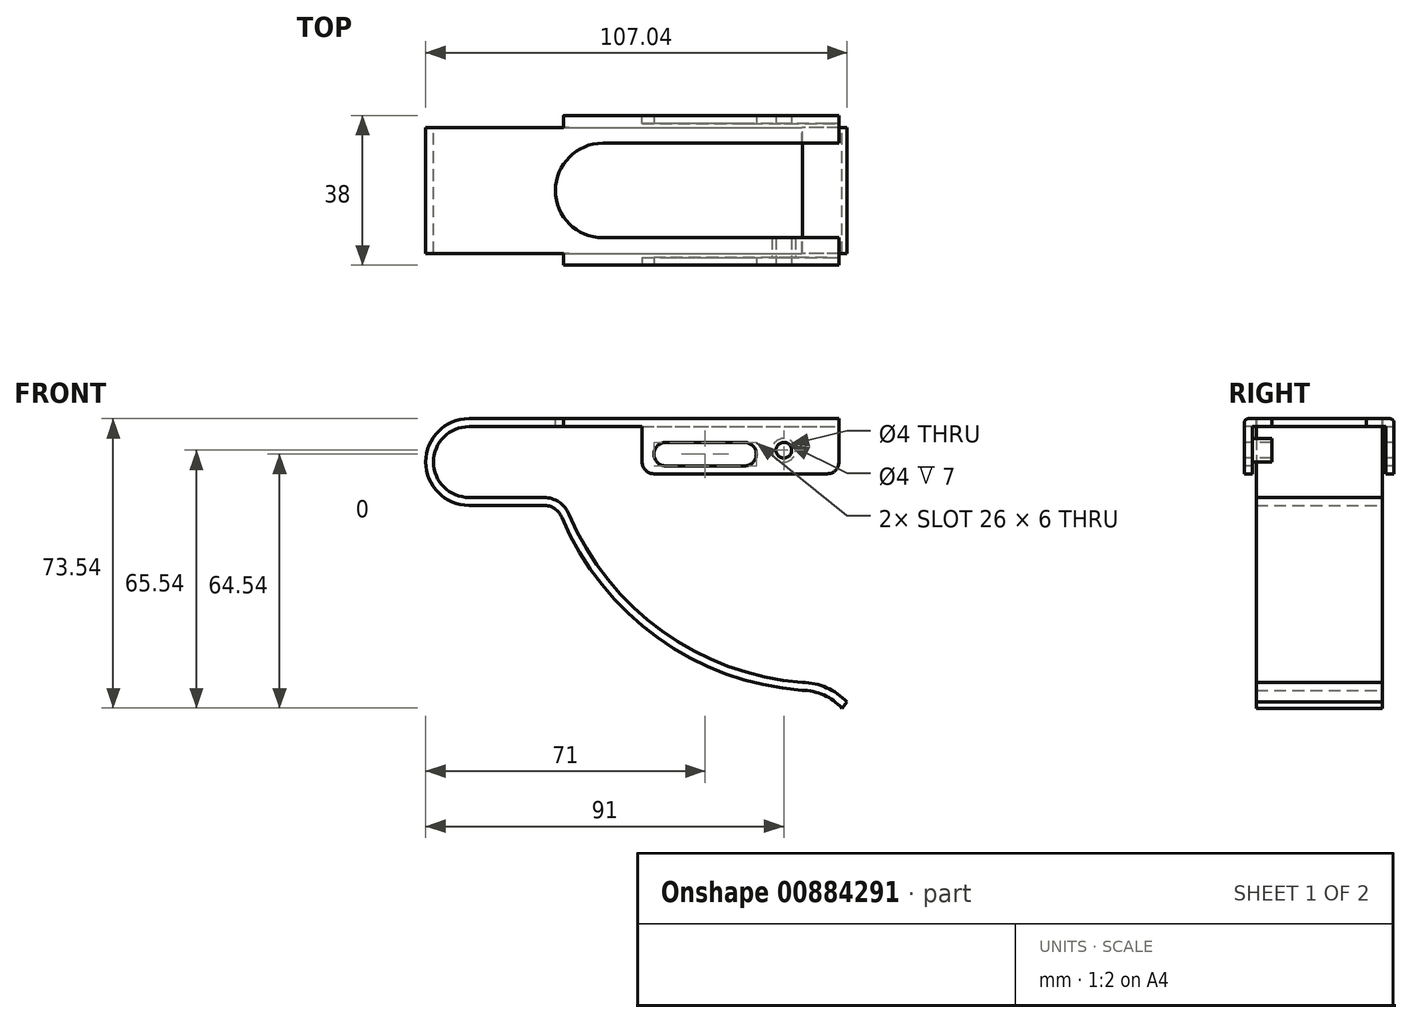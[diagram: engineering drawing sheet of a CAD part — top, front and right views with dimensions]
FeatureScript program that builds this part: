
annotation { "Feature Type Name" : "Feature", "Feature Type Description" : "" }
export const myFeature = defineFeature(function(context is Context, id is Id, definition is map)
    precondition{}
    {
        {
            var Q0;
            Q0=qCreatedBy(makeId("Front.planeOp"),FACE);
            var sketch = newSketch(context, id + "F0", { "sketchPlane" : qUnion([Q0])});
            skArc(sketch, "E0", {"start": v(0, 11) * mm, "mid": v(-11, 0) * mm, "end": v(0, -11) * mm});
            skLineSegment(sketch, "E1", {"start": v(0, 11) * mm, "end": v(94, 11) * mm});
            skLineSegment(sketch, "E2", {"start": v(0, -11) * mm, "end": v(19, -11) * mm});
            skArc(sketch, "E3", {"start": v(23.61, -14.06) * mm, "mid": v(47.92, -44.63) * mm, "end": v(84.61, -58) * mm});
            skPoint(sketch, "E4.visualSharp", {"position": v(22.4, -11) * mm});
            skArc(sketch, "E4.filletArc", {"start": v(23.61, -14.06) * mm, "mid": v(21.77, -11.84) * mm, "end": v(19, -11) * mm});
            skArc(sketch, "E5", {"start": v(94.75, -62.54) * mm, "mid": v(90.15, -59.22) * mm, "end": v(84.61, -58) * mm});
            skLineSegment(sketch, "E6.0", {"start": v(0, 9) * mm, "end": v(94, 9) * mm});
            skArc(sketch, "E6.1", {"start": v(0, 9) * mm, "mid": v(-9, 0) * mm, "end": v(0, -9) * mm});
            skArc(sketch, "E6.2", {"start": v(96.04, -61) * mm, "mid": v(90.88, -57.36) * mm, "end": v(84.7, -56) * mm});
            skArc(sketch, "E6.3", {"start": v(25.45, -13.3) * mm, "mid": v(49.07, -42.99) * mm, "end": v(84.7, -56) * mm});
            skArc(sketch, "E6.4", {"start": v(25.45, -13.3) * mm, "mid": v(22.88, -10.17) * mm, "end": v(19, -9) * mm});
            skLineSegment(sketch, "E6.5", {"start": v(0, -9) * mm, "end": v(19, -9) * mm});
            skLineSegment(sketch, "E7", {"start": v(94, 11) * mm, "end": v(94, 9) * mm});
            skLineSegment(sketch, "E8", {"start": v(96.04, -61) * mm, "end": v(94.75, -62.54) * mm});
            skLineSegment(sketch, "E9", {"start": v(96.04, -61) * mm, "end": v(104.04, -61) * mm, "construction": true});
            skSolve(sketch);
        }
        {
            var Q0;
            Q0=qSketchRegion(id+"F0",true);
            extrude(context, id + "F1", {"entities" : qUnion([Q0]), "depth" : 16 * mm, "offsetDistance" : 25 * mm});
        }
        {
            var Q0;
            Q0=makeQuery(id+"F1.opExtrude","SWEPT_FACE",FACE,{"disambiguationData":[OSD([sQuery(id+"F0.wireOp",EDGE,"E1")])]});
            var sketch = newSketch(context, id + "F2", { "sketchPlane" : qUnion([Q0])});
            skLineSegment(sketch, "E10.bottom", {"start": v(94, -16) * mm, "end": v(24, -16) * mm});
            skLineSegment(sketch, "E10.top", {"start": v(94, -19) * mm, "end": v(24, -19) * mm});
            skLineSegment(sketch, "E10.left", {"start": v(94, -16) * mm, "end": v(94, -19) * mm});
            skLineSegment(sketch, "E10.right", {"start": v(24, -16) * mm, "end": v(24, -19) * mm});
            skSolve(sketch);
        }
        {
            var Q0;
            Q0=qSketchRegion(id+"F2",true);
            extrude(context, id + "F3", {"entities" : qUnion([Q0]), "operationType" : NewBodyOperationType.ADD, "oppositeDirection" : true, "depth" : 2 * mm, "offsetDistance" : 25 * mm});
        }
        {
            var Q0;
            Q0=makeQuery(id+"F3.opExtrude","SWEPT_FACE",FACE,{"disambiguationData":[OSD([sQuery(id+"F2.wireOp",EDGE,"E10.top")])]});
            var sketch = newSketch(context, id + "F4", { "sketchPlane" : qUnion([Q0])});
            skLineSegment(sketch, "E11.bottom", {"start": v(94, 11) * mm, "end": v(44, 11) * mm});
            skLineSegment(sketch, "E11.top", {"start": v(94, -3) * mm, "end": v(44, -3) * mm});
            skLineSegment(sketch, "E11.left", {"start": v(94, 11) * mm, "end": v(94, -3) * mm});
            skLineSegment(sketch, "E11.right", {"start": v(44, 11) * mm, "end": v(44, -3) * mm});
            skSolve(sketch);
        }
        {
            var Q0;
            Q0=qSketchRegion(id+"F4",true);
            extrude(context, id + "F5", {"entities" : qUnion([Q0]), "operationType" : NewBodyOperationType.ADD, "oppositeDirection" : true, "depth" : 2 * mm, "offsetDistance" : 25 * mm});
        }
        {
            var Q0;
            Q0=makeQuery(id+"F3.opExtrude","CAP_EDGE",EDGE,{"disambiguationData":[OSD([sQuery(id+"F2.wireOp",EDGE,"E10.top")])],"isStart":true});
            fillet(context, id + "F6", {"entities" : qUnion([Q0]), "radius" : 1 * mm, "allowEdgeOverflow" : false});
        }
        {
            var Q0;
            Q0=makeQuery(id+"F1.opExtrude","SWEPT_BODY",BODY,{"disambiguationData":[OSD([sQuery(id+"F0.wireOp",EDGE,"E0"),sQuery(id+"F0.wireOp",EDGE,"E1"),sQuery(id+"F0.wireOp",EDGE,"E2"),sQuery(id+"F0.wireOp",EDGE,"E3"),sQuery(id+"F0.wireOp",EDGE,"E4.filletArc"),sQuery(id+"F0.wireOp",EDGE,"E5"),sQuery(id+"F0.wireOp",EDGE,"E6.0"),sQuery(id+"F0.wireOp",EDGE,"E6.1"),sQuery(id+"F0.wireOp",EDGE,"E6.2"),sQuery(id+"F0.wireOp",EDGE,"E6.3"),sQuery(id+"F0.wireOp",EDGE,"E6.4"),sQuery(id+"F0.wireOp",EDGE,"E6.5"),sQuery(id+"F0.wireOp",EDGE,"E7"),sQuery(id+"F0.wireOp",EDGE,"E8")])]});
            var Q1;
            Q1=qCreatedBy(makeId("Front.planeOp"),FACE);
            mirror(context, id + "F7", {"operationType" : NewBodyOperationType.ADD, "entities" : qUnion([Q0]), "mirrorPlane" : qUnion([Q1])});
        }
        {
            var Q0;
            {var subQ0=makeQuery(id+"F3.boolean.opBoolean","MERGE",FACE,{"derivedFrom":[makeQuery(id+"F1.opExtrude","SWEPT_FACE",FACE,{"disambiguationData":[OSD([sQuery(id+"F0.wireOp",EDGE,"E1")])]}),makeQuery(id+"F3.opExtrude","CAP_FACE",FACE,{"disambiguationData":[OSD([sQuery(id+"F2.wireOp",EDGE,"E10.bottom"),sQuery(id+"F2.wireOp",EDGE,"E10.top"),sQuery(id+"F2.wireOp",EDGE,"E10.left"),sQuery(id+"F2.wireOp",EDGE,"E10.right")])],"isStart":true})]});Q0=makeQuery(id+"F7.boolean.opBoolean","MERGE",FACE,{"derivedFrom":[subQ0,makeQuery(id+"F7.opPattern","COPY",FACE,{"derivedFrom":subQ0,"instanceName":"1"})]});}
            var sketch = newSketch(context, id + "F8", { "sketchPlane" : qUnion([Q0])});
            skArc(sketch, "E12", {"start": v(34, 12) * mm, "mid": v(22, 0) * mm, "end": v(34, -12) * mm});
            skLineSegment(sketch, "E13", {"start": v(34, 12) * mm, "end": v(94, 12) * mm});
            skLineSegment(sketch, "E14", {"start": v(34, -12) * mm, "end": v(94, -12) * mm});
            skLineSegment(sketch, "E15", {"start": v(94, 12) * mm, "end": v(94, -12) * mm});
            skSolve(sketch);
        }
        {
            var Q0;
            Q0=qSketchRegion(id+"F8",true);
            extrude(context, id + "F9", {"entities" : qUnion([Q0]), "operationType" : NewBodyOperationType.REMOVE, "oppositeDirection" : true, "depth" : 2 * mm, "offsetDistance" : 25 * mm});
        }
        {
            var Q0;
            Q0=makeQuery(id+"F5.boolean.opBoolean","MERGE",FACE,{"derivedFrom":[makeQuery(id+"F3.opExtrude","SWEPT_FACE",FACE,{"disambiguationData":[OSD([sQuery(id+"F2.wireOp",EDGE,"E10.top")])]}),makeQuery(id+"F5.opExtrude","CAP_FACE",FACE,{"disambiguationData":[OSD([sQuery(id+"F4.wireOp",EDGE,"E11.bottom"),sQuery(id+"F4.wireOp",EDGE,"E11.top"),sQuery(id+"F4.wireOp",EDGE,"E11.left"),sQuery(id+"F4.wireOp",EDGE,"E11.right")])],"isStart":true})]});
            var sketch = newSketch(context, id + "F10", { "sketchPlane" : qUnion([Q0])});
            skLineSegment(sketch, "E16", {"start": v(50, 2) * mm, "end": v(70, 2) * mm});
            skArc(sketch, "E17.0.startCap", {"start": v(50, -1) * mm, "mid": v(47, 2) * mm, "end": v(50, 5) * mm});
            skArc(sketch, "E17.0.endCap", {"start": v(70, 5) * mm, "mid": v(73, 2) * mm, "end": v(70, -1) * mm});
            skLineSegment(sketch, "E17.0.left", {"start": v(50, 5) * mm, "end": v(70, 5) * mm});
            skLineSegment(sketch, "E17.0.right", {"start": v(50, -1) * mm, "end": v(70, -1) * mm});
            skSolve(sketch);
        }
        {
            var Q0;
            Q0=qSketchRegion(id+"F10",true);
            extrude(context, id + "F11", {"entities" : qUnion([Q0]), "operationType" : NewBodyOperationType.REMOVE, "endBound" : BoundingType.THROUGH_ALL, "oppositeDirection" : true, "depth" : 25 * mm, "offsetDistance" : 25 * mm});
        }
        {
            var Q0;
            Q0=makeQuery(id+"F5.boolean.opBoolean","MERGE",FACE,{"derivedFrom":[makeQuery(id+"F3.opExtrude","SWEPT_FACE",FACE,{"disambiguationData":[OSD([sQuery(id+"F2.wireOp",EDGE,"E10.top")])]}),makeQuery(id+"F5.opExtrude","CAP_FACE",FACE,{"disambiguationData":[OSD([sQuery(id+"F4.wireOp",EDGE,"E11.bottom"),sQuery(id+"F4.wireOp",EDGE,"E11.top"),sQuery(id+"F4.wireOp",EDGE,"E11.left"),sQuery(id+"F4.wireOp",EDGE,"E11.right")])],"isStart":true})]});
            var sketch = newSketch(context, id + "F12", { "sketchPlane" : qUnion([Q0])});
            skPoint(sketch, "E18", {"position": v(80, 3) * mm});
            skSolve(sketch);
        }
        {
            var Q0;
            Q0=sQuery(id+"F12.wireOp",VERTEX,"E18");
            var Q1;
            Q1=makeQuery(id+"F1.opExtrude","SWEPT_BODY",BODY,{"disambiguationData":[OSD([sQuery(id+"F0.wireOp",EDGE,"E0"),sQuery(id+"F0.wireOp",EDGE,"E1"),sQuery(id+"F0.wireOp",EDGE,"E2"),sQuery(id+"F0.wireOp",EDGE,"E3"),sQuery(id+"F0.wireOp",EDGE,"E4.filletArc"),sQuery(id+"F0.wireOp",EDGE,"E5"),sQuery(id+"F0.wireOp",EDGE,"E6.0"),sQuery(id+"F0.wireOp",EDGE,"E6.1"),sQuery(id+"F0.wireOp",EDGE,"E6.2"),sQuery(id+"F0.wireOp",EDGE,"E6.3"),sQuery(id+"F0.wireOp",EDGE,"E6.4"),sQuery(id+"F0.wireOp",EDGE,"E6.5"),sQuery(id+"F0.wireOp",EDGE,"E7"),sQuery(id+"F0.wireOp",EDGE,"E8")])]});
            hole(context, id + "F13", {"style" : HoleStyle.SIMPLE, "endStyle" : HoleEndStyle.THROUGH, "holeDiameter" : 4 * mm, "majorDiameter" : 5 * mm, "isTappedThrough" : true, "tappedDepth" : 12 * mm, "tapClearance" : 3, "locations" : qUnion([Q0]), "scope" : qUnion([Q1])});
        }
        {
            var Q0;
            Q0=makeQuery(id+"F5.opExtrude","CAP_FACE",FACE,{"disambiguationData":[OSD([sQuery(id+"F4.wireOp",EDGE,"E11.bottom"),sQuery(id+"F4.wireOp",EDGE,"E11.top"),sQuery(id+"F4.wireOp",EDGE,"E11.left"),sQuery(id+"F4.wireOp",EDGE,"E11.right")])],"isStart":false});
            var sketch = newSketch(context, id + "F14", { "sketchPlane" : qUnion([Q0])});
            skCircle(sketch, "E19.0", {"center": v(-80, 3) * mm, "radius": 2 * mm});
            skCircle(sketch, "E20.0", {"center": v(-80, 3) * mm, "radius": 3 * mm});
            skSolve(sketch);
        }
        {
            var Q0;
            Q0=qSketchRegion(id+"F14",true);
            extrude(context, id + "F15", {"entities" : qUnion([Q0]), "operationType" : NewBodyOperationType.ADD, "depth" : 5 * mm, "offsetDistance" : 25 * mm});
        }
        {
            var Q0;
            Q0=makeQuery(id+"F7.opPattern","COPY",EDGE,{"derivedFrom":makeQuery(id+"F5.opExtrude","SWEPT_EDGE",EDGE,{"disambiguationData":[OSD([sQuery(id+"F4.wireOp",EDGE,"E11.top"),sQuery(id+"F4.wireOp",EDGE,"E11.left")])]}),"instanceName":"1"});
            var Q1;
            Q1=makeQuery(id+"F7.opPattern","COPY",EDGE,{"derivedFrom":makeQuery(id+"F5.opExtrude","SWEPT_EDGE",EDGE,{"disambiguationData":[OSD([sQuery(id+"F4.wireOp",EDGE,"E11.top"),sQuery(id+"F4.wireOp",EDGE,"E11.right")])]}),"instanceName":"1"});
            var Q2;
            Q2=makeQuery(id+"F5.opExtrude","SWEPT_EDGE",EDGE,{"disambiguationData":[OSD([sQuery(id+"F4.wireOp",EDGE,"E11.top"),sQuery(id+"F4.wireOp",EDGE,"E11.right")])]});
            var Q3;
            Q3=makeQuery(id+"F5.opExtrude","SWEPT_EDGE",EDGE,{"disambiguationData":[OSD([sQuery(id+"F4.wireOp",EDGE,"E11.top"),sQuery(id+"F4.wireOp",EDGE,"E11.left")])]});
            fillet(context, id + "F16", {"entities" : qUnion([Q0, Q1, Q2, Q3]), "radius" : 3 * mm, "tangentPropagation" : true, "allowEdgeOverflow" : false});
        }
    });
